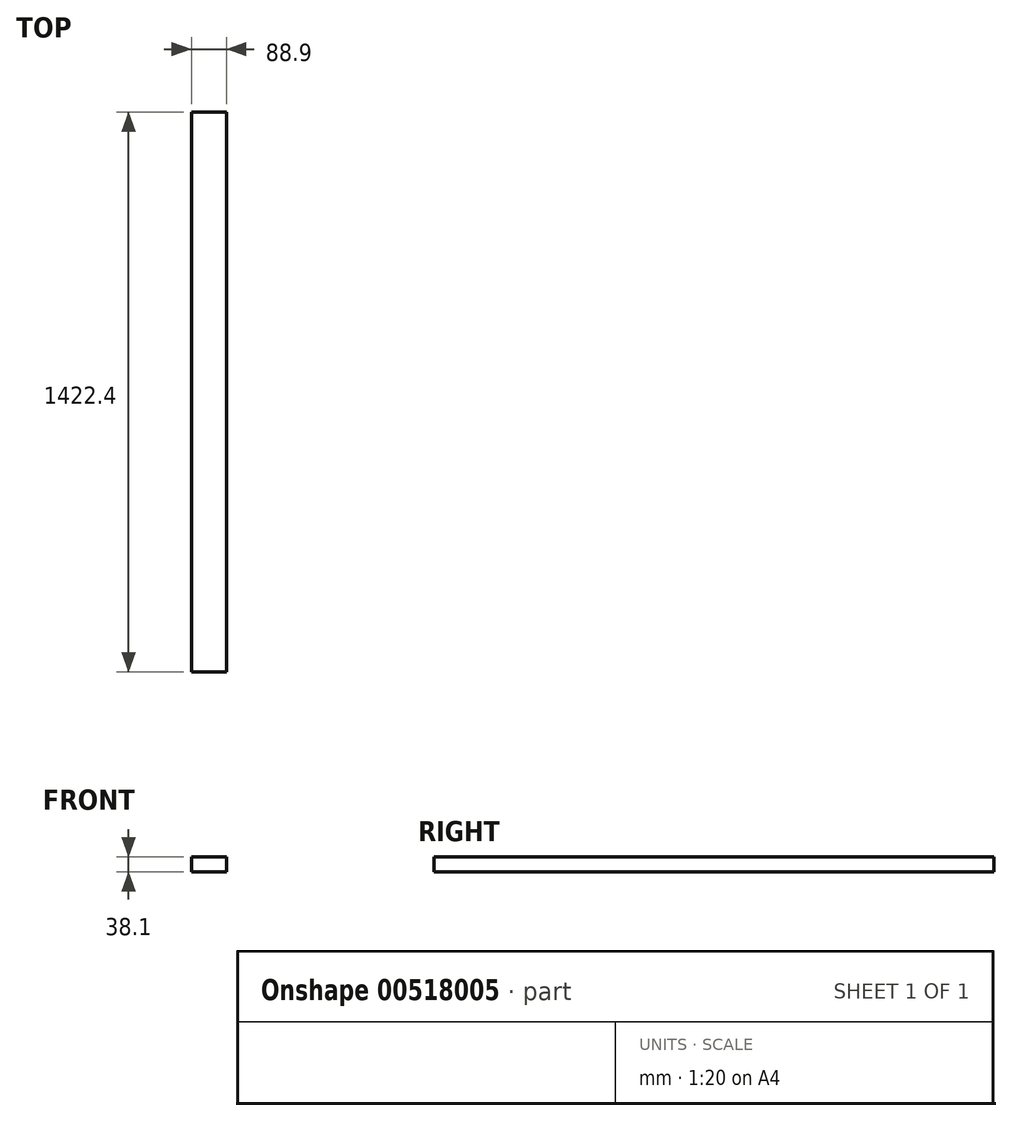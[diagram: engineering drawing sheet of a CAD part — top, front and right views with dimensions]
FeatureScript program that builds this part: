
annotation { "Feature Type Name" : "Feature", "Feature Type Description" : "" }
export const myFeature = defineFeature(function(context is Context, id is Id, definition is map)
    precondition{}
    {
        {
            var Q0;
            Q0=qCreatedBy(makeId("Front.planeOp"),FACE);
            var sketch = newSketch(context, id + "F0", { "sketchPlane" : qUnion([Q0])});
            skLineSegment(sketch, "E0.bottom", {"start": v(0, 0) * mm, "end": v(88.9, 0) * mm});
            skLineSegment(sketch, "E0.top", {"start": v(0, 38.1) * mm, "end": v(88.9, 38.1) * mm});
            skLineSegment(sketch, "E0.left", {"start": v(0, 0) * mm, "end": v(0, 38.1) * mm});
            skLineSegment(sketch, "E0.right", {"start": v(88.9, 0) * mm, "end": v(88.9, 38.1) * mm});
            skSolve(sketch);
        }
        {
            var Q0;
            Q0=qSketchRegion(id+"F0",true);
            extrude(context, id + "F1", {"entities" : qUnion([Q0]), "depth" : 1422.4 * mm, "offsetDistance" : 25 * mm});
        }
    });
